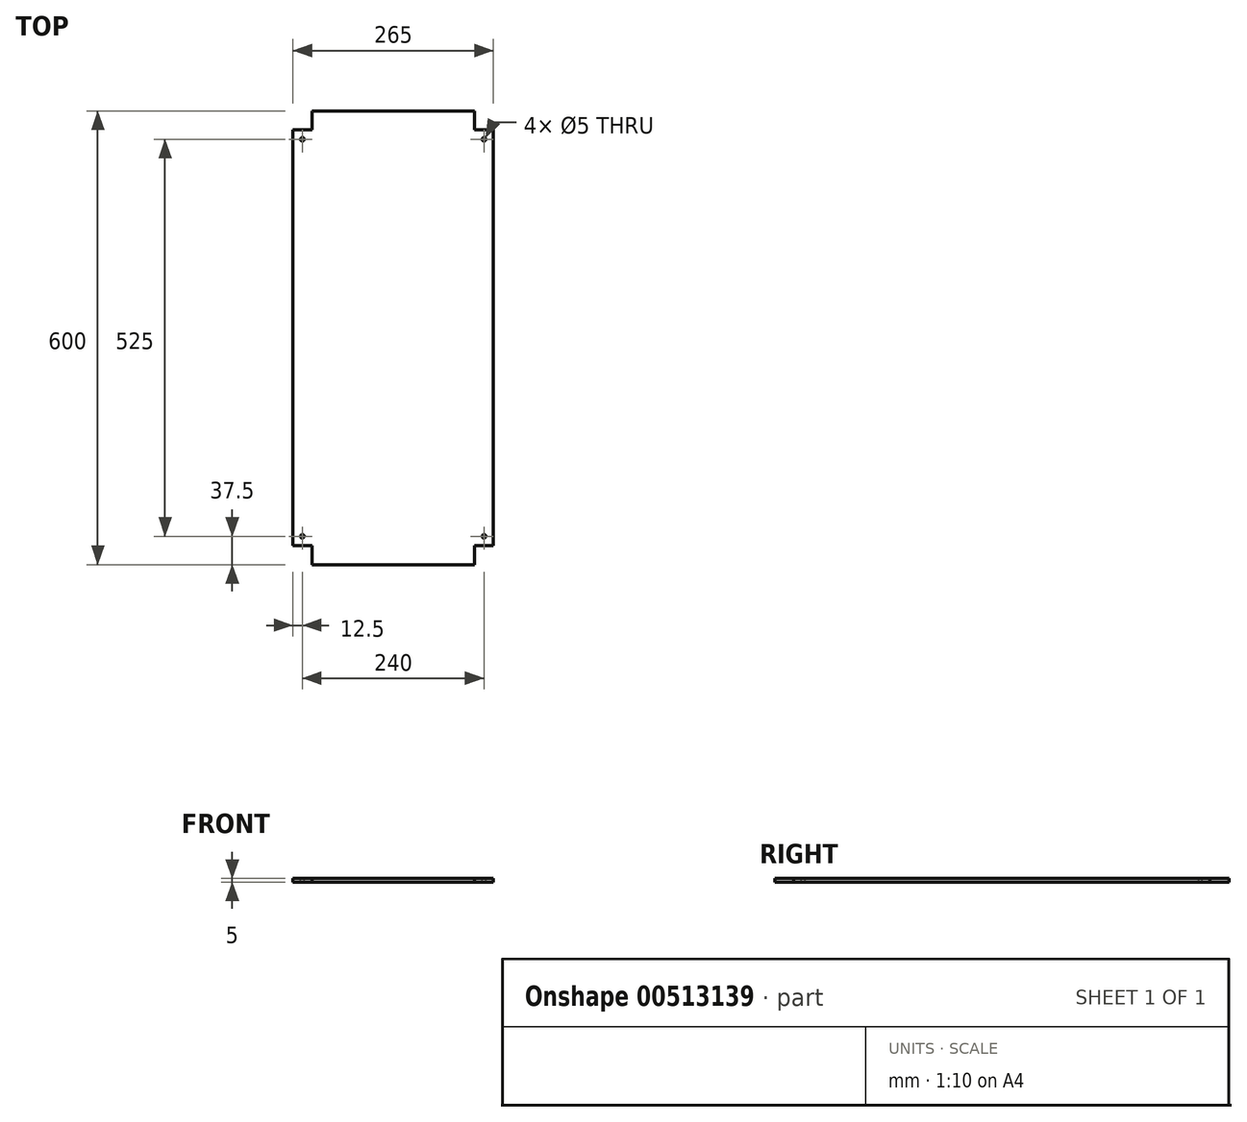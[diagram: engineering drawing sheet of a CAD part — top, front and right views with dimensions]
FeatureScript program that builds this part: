
annotation { "Feature Type Name" : "Feature", "Feature Type Description" : "" }
export const myFeature = defineFeature(function(context is Context, id is Id, definition is map)
    precondition{}
    {
        {
            var Q0;
            Q0=qCreatedBy(makeId("Top.planeOp"),FACE);
            var sketch = newSketch(context, id + "F0", { "sketchPlane" : qUnion([Q0])});
            skLineSegment(sketch, "E0.bottom", {"start": v(107.5, 300) * mm, "end": v(-107.5, 300) * mm});
            skLineSegment(sketch, "E0.top", {"start": v(107.5, -300) * mm, "end": v(-107.5, -300) * mm});
            skLineSegment(sketch, "E0.left", {"start": v(132.5, 275) * mm, "end": v(132.5, -275) * mm});
            skLineSegment(sketch, "E0.right", {"start": v(-132.5, 275) * mm, "end": v(-132.5, -275) * mm});
            skPoint(sketch, "E0.middle", {"position": v(0, 0) * mm});
            skLineSegment(sketch, "E1", {"start": v(-107.5, 300) * mm, "end": v(-107.5, 275) * mm});
            skLineSegment(sketch, "E2", {"start": v(-107.5, 275) * mm, "end": v(-132.5, 275) * mm});
            skLineSegment(sketch, "E3", {"start": v(107.5, 300) * mm, "end": v(107.5, 275) * mm});
            skLineSegment(sketch, "E4", {"start": v(107.5, 275) * mm, "end": v(132.5, 275) * mm});
            skLineSegment(sketch, "E5", {"start": v(-132.5, -275) * mm, "end": v(-107.5, -275) * mm});
            skLineSegment(sketch, "E6", {"start": v(-107.5, -275) * mm, "end": v(-107.5, -300) * mm});
            skLineSegment(sketch, "E7", {"start": v(107.5, -300) * mm, "end": v(107.5, -275) * mm});
            skLineSegment(sketch, "E8", {"start": v(107.5, -275) * mm, "end": v(132.5, -275) * mm});
            skPoint(sketch, "E9.orphan", {"position": v(-132.5, 300) * mm});
            skPoint(sketch, "E10.orphan", {"position": v(132.5, 300) * mm});
            skPoint(sketch, "E11.orphan", {"position": v(-132.5, -300) * mm});
            skPoint(sketch, "E12.orphan", {"position": v(132.5, -300) * mm});
            skSolve(sketch);
        }
        {
            var Q0;
            Q0=makeQuery(id+"F0.imprint","IMPRINT",FACE,{"disambiguationData":[TD([[makeQuery(id+"F0.imprint","IMPRINT",EDGE,{"derivedFrom":sQuery(id+"F0.wireOp",EDGE,"E0.bottom")}),1.0]])]});
            extrude(context, id + "F1", {"entities" : qUnion([Q0]), "depth" : 5 * mm, "offsetDistance" : 25 * mm});
        }
        {
            var Q0;
            Q0=makeQuery(id+"F1.opExtrude","CAP_FACE",FACE,{"disambiguationData":[OSD([sQuery(id+"F0.wireOp",EDGE,"E0.bottom"),sQuery(id+"F0.wireOp",EDGE,"E0.top"),sQuery(id+"F0.wireOp",EDGE,"E0.left"),sQuery(id+"F0.wireOp",EDGE,"E0.right"),sQuery(id+"F0.wireOp",EDGE,"E1"),sQuery(id+"F0.wireOp",EDGE,"E2"),sQuery(id+"F0.wireOp",EDGE,"E3"),sQuery(id+"F0.wireOp",EDGE,"E4"),sQuery(id+"F0.wireOp",EDGE,"E5"),sQuery(id+"F0.wireOp",EDGE,"E6"),sQuery(id+"F0.wireOp",EDGE,"E7"),sQuery(id+"F0.wireOp",EDGE,"E8")])],"isStart":false});
            var sketch = newSketch(context, id + "F2", { "sketchPlane" : qUnion([Q0])});
            skPoint(sketch, "E13", {"position": v(-120, 262.5) * mm});
            skPoint(sketch, "E14", {"position": v(120, 262.5) * mm});
            skPoint(sketch, "E15", {"position": v(-120, -262.5) * mm});
            skPoint(sketch, "E16", {"position": v(120, -262.5) * mm});
            skSolve(sketch);
        }
        {
            var Q0;
            Q0=sQuery(id+"F2.wireOp",VERTEX,"E13");
            var Q1;
            Q1=sQuery(id+"F2.wireOp",VERTEX,"E14");
            var Q2;
            Q2=sQuery(id+"F2.wireOp",VERTEX,"E15");
            var Q3;
            Q3=sQuery(id+"F2.wireOp",VERTEX,"E16");
            var Q4;
            Q4=makeQuery(id+"F1.opExtrude","SWEPT_BODY",BODY,{"disambiguationData":[OSD([sQuery(id+"F0.wireOp",EDGE,"E0.bottom"),sQuery(id+"F0.wireOp",EDGE,"E0.top"),sQuery(id+"F0.wireOp",EDGE,"E0.left"),sQuery(id+"F0.wireOp",EDGE,"E0.right"),sQuery(id+"F0.wireOp",EDGE,"E1"),sQuery(id+"F0.wireOp",EDGE,"E2"),sQuery(id+"F0.wireOp",EDGE,"E3"),sQuery(id+"F0.wireOp",EDGE,"E4"),sQuery(id+"F0.wireOp",EDGE,"E5"),sQuery(id+"F0.wireOp",EDGE,"E6"),sQuery(id+"F0.wireOp",EDGE,"E7"),sQuery(id+"F0.wireOp",EDGE,"E8")])]});
            hole(context, id + "F3", {"style" : HoleStyle.SIMPLE, "endStyle" : HoleEndStyle.THROUGH, "holeDiameter" : 5 * mm, "isTappedThrough" : true, "tappedDepth" : 12 * mm, "tapClearance" : 3, "startFromSketch" : true, "locations" : qUnion([Q0, Q1, Q2, Q3]), "scope" : qUnion([Q4])});
        }
    });
